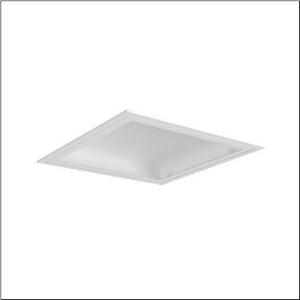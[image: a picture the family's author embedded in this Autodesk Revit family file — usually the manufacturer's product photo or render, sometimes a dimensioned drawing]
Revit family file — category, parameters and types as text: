
# Revit family: mira_r__21_51fr427a462a_66f5
name_source: partatom
category: Lighting Fixtures
units: mm (PartAtom-declared; Revit-internal decimal feet)

## family parameters
Cut with Voids When Loaded = No
Host = Face
Light Source = No
Part Type = Normal
Room Calculation Point = No
Round Connector Dimension = Use Diameter
Shared = No

## types (1)
- Mira® 21 (1 x LED, 6420 lm, 53 W, 4000K)
    Apparent Load = 53 VA
    CIE Flux Codes = 50 81 97 100 100
    Color Rendering = 80
    Color Temperature = 4000K
    Default Elevation = 1800 mm
    Description = Mira® 21, clean room luminaire, primary light control with reflector, primary optical cover: cover, of PC, light emission: direct distribution, primary light characteristic: symmetric, installation type: recessed, LED, rated luminous flux: 6.420lm, luminous efficacy: 121lm/W, light colour: 840, colour temperature: 4000K, control gear: ON/OFF, with terminal, 3-pole, max. 2.5mm², mains connection: 230V, AC, 50/60Hz, rated input power: 53W, luminaire housing, of sheet steel, coated, pure white (RAL 9010), with concealed spring brackets, module: M625, length: 623mm, width: 623mm, height: 115mm, protection rating (complete): IP54, insulation class (complete): insulation class I (protective earthing), certification: CE, UKCA, permissible operating ambient temperature: -5..+40°C, standard: EN 50419, packaging unit: 1 piece
    Height = 0 mm  [stored 0 ft]
    Lamp = 1 x LED
    Lamp Light Flux = 6420 lm
    Lamp Power = 53 W
    Lamp count = 1
    Length = 625 mm
    Luminous efficacy = 121 lm/W
    Manufacturer = Siteco
    ModVariant = No
    Model = 51FR427A462A
    Mounting Place = Ceiling
    Mounting Type = Recessed
    Number of Poles = 1
    OnlyDefault = Yes
    Power Factor = 1
    Product Name = Mira® 21
    Product group = clean room luminaire | ceiling recessed
    ProductGroupID = 402
    Protection Class = Protection class I
    Protection Degree = IP 54
    RLX_Detail_Level = 1
    RLX_Emergency_Light_Flux = 0 lm
    RLX_Emergency_Type = 0
    RLX_Emergency_Type_DB = No
    RlxData = <blob elided: 13405 chars, md5=bc86cd86>
    Socket = socket
    Standby Power = 0 W
    System Light Flux = 6420 lm
    System Power = 53 W
    Type Comments = Product without accessories
    Type Image = l_1007109.jpg
    URL = http://relux.com
    VarID = ---
    Voltage = 0 V
    Weight = 0.00 kg
    Width = 625 mm

note: [stored X ft] marks values corroborated as IEEE doubles in the binary element streams (Revit-internal decimal feet)

## geometry (parser evidence)
native form markers: Sweep x11
no freeform markers — native parametric forms only
